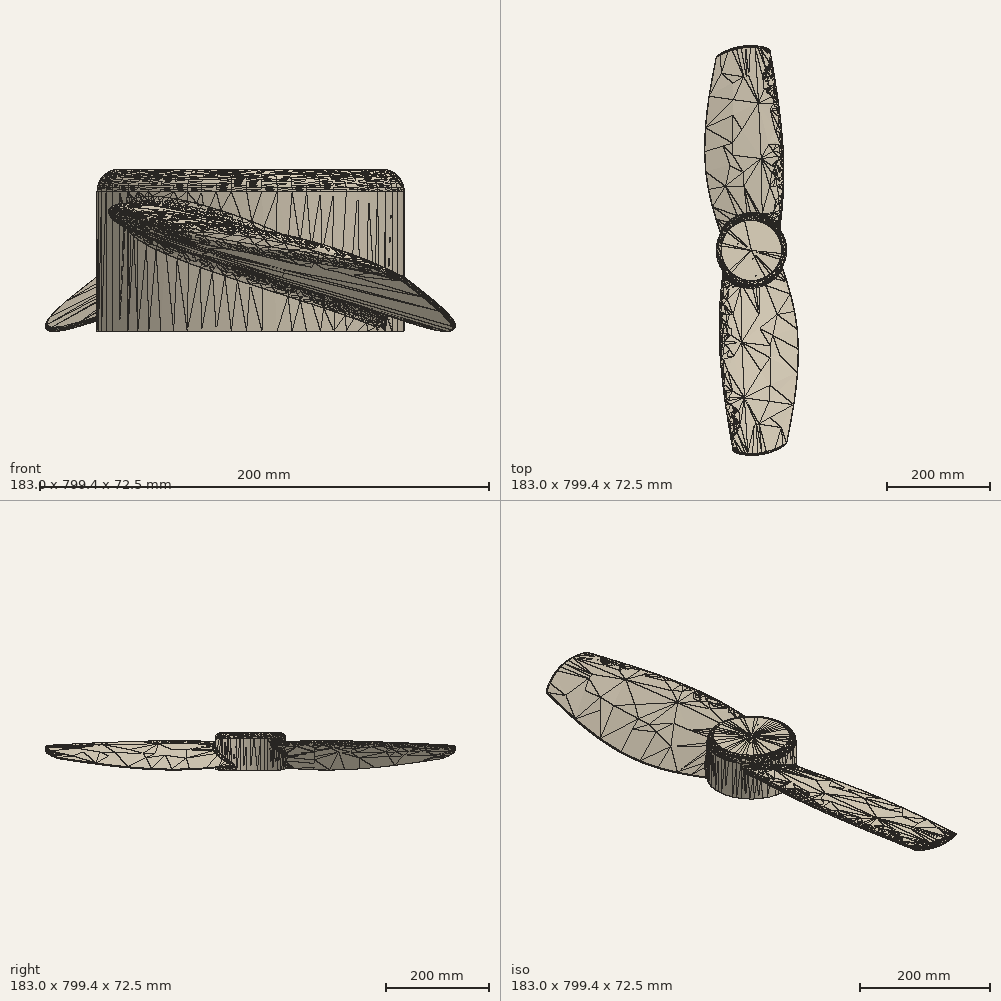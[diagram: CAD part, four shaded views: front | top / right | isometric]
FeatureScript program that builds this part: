
annotation { "Feature Type Name" : "Feature", "Feature Type Description" : "" }
export const myFeature = defineFeature(function(context is Context, id is Id, definition is map)
    precondition{}
    {
        {
            var Q0;
            Q0=qCreatedBy(makeId("Front.planeOp"),FACE);
            var sketch = newSketch(context, id + "F0", { "sketchPlane" : qUnion([Q0])});
            skLineSegment(sketch, "E0", {"start": v(-25.68, 10.16) * mm, "end": v(0, 0) * mm, "construction": true});
            skLineSegment(sketch, "E1", {"start": v(0, 0) * mm, "end": v(25.68, -10.16) * mm, "construction": true});
            skLineSegment(sketch, "E2", {"start": v(25.68, -10.16) * mm, "end": v(51.36, -20.31) * mm, "construction": true});
            skLineSegment(sketch, "E3", {"start": v(51.36, -20.31) * mm, "end": v(77.03, -30.47) * mm, "construction": true});
            skLineSegment(sketch, "E4", {"start": v(0, 0) * mm, "end": v(3.73, 9.44) * mm, "construction": true});
            skLineSegment(sketch, "E5", {"start": v(-25.68, 10.16) * mm, "end": v(-23.81, 14.88) * mm, "construction": true});
            skFitSpline(sketch, "E6", {"points": [v(-25.68, 10.16) * mm, v(3.73, 9.44) * mm, v(77.03, -30.47) * mm], "startDerivative": vector(15.03, 38) * mm, "endDerivative": vector(104.92, -93.69) * mm});
            skPoint(sketch, "E7", {"position": v(1.87, 4.72) * mm});
            skLineSegment(sketch, "E8", {"start": v(-23.81, 14.88) * mm, "end": v(1.87, 4.72) * mm, "construction": true});
            skLineSegment(sketch, "E9", {"start": v(0, 0) * mm, "end": v(-1.87, -4.72) * mm, "construction": true});
            skLineSegment(sketch, "E10", {"start": v(-25.68, 10.16) * mm, "end": v(-27.54, 5.44) * mm, "construction": true});
            skFitSpline(sketch, "E11", {"points": [v(-25.68, 10.16) * mm, v(-1.87, -4.72) * mm, v(77.03, -30.47) * mm], "startDerivative": vector(-15.23, -38.5) * mm, "endDerivative": vector(121.84, -48.19) * mm});
            skLineSegment(sketch, "E12", {"start": v(51.36, -20.31) * mm, "end": v(55.09, -10.87) * mm, "construction": true});
            skSolve(sketch);
        }
        {
            var Q0;
            Q0=qCreatedBy(makeId("Front.planeOp"),FACE);
            cPlane(context, id + "F1", {"entities" : qUnion([Q0]), "cplaneType" : CPlaneType.OFFSET, "offset" : 125 * mm, "width" : 150 * mm, "height" : 150 * mm});
        }
        {
            var Q0;
            Q0=qCreatedBy(id+"F1.planeOp",FACE);
            var sketch = newSketch(context, id + "F2", { "sketchPlane" : qUnion([Q0])});
            skLineSegment(sketch, "E13", {"start": v(-38.33, 14.06) * mm, "end": v(0, 0) * mm, "construction": true});
            skLineSegment(sketch, "E14", {"start": v(0, 0) * mm, "end": v(38.33, -14.06) * mm, "construction": true});
            skLineSegment(sketch, "E15", {"start": v(38.33, -14.06) * mm, "end": v(76.67, -28.12) * mm, "construction": true});
            skLineSegment(sketch, "E16", {"start": v(76.67, -28.12) * mm, "end": v(115, -42.17) * mm, "construction": true});
            skLineSegment(sketch, "E17", {"start": v(0, 0) * mm, "end": v(4.06, 11.06) * mm, "construction": true});
            skLineSegment(sketch, "E18", {"start": v(-38.33, 14.06) * mm, "end": v(-36.3, 19.59) * mm, "construction": true});
            skFitSpline(sketch, "E19", {"points": [v(-38.33, 14.06) * mm, v(4.06, 11.06) * mm, v(115, -42.17) * mm], "startDerivative": vector(16.44, 44.82) * mm, "endDerivative": vector(163.27, -119.63) * mm});
            skPoint(sketch, "E20", {"position": v(2.03, 5.53) * mm});
            skLineSegment(sketch, "E21", {"start": v(-36.3, 19.59) * mm, "end": v(2.03, 5.53) * mm, "construction": true});
            skLineSegment(sketch, "E22", {"start": v(0, 0) * mm, "end": v(-2.03, -5.53) * mm, "construction": true});
            skLineSegment(sketch, "E23", {"start": v(-38.33, 14.06) * mm, "end": v(-40.36, 8.53) * mm, "construction": true});
            skFitSpline(sketch, "E24", {"points": [v(-38.33, 14.06) * mm, v(-2.03, -5.53) * mm, v(115, -42.17) * mm], "startDerivative": vector(-16.57, -45.19) * mm, "endDerivative": vector(181.7, -66.64) * mm});
            skLineSegment(sketch, "E25", {"start": v(76.67, -28.12) * mm, "end": v(80.72, -17.06) * mm, "construction": true});
            skSolve(sketch);
        }
        {
            var Q0;
            Q0=qCreatedBy(makeId("Front.planeOp"),FACE);
            cPlane(context, id + "F3", {"entities" : qUnion([Q0]), "cplaneType" : CPlaneType.OFFSET, "offset" : 400 * mm, "width" : 150 * mm, "height" : 150 * mm});
        }
        {
            var Q0;
            Q0=qCreatedBy(id+"F3.planeOp",FACE);
            var sketch = newSketch(context, id + "F4", { "sketchPlane" : qUnion([Q0])});
            skLineSegment(sketch, "E26", {"start": v(-10.03, 5.14) * mm, "end": v(16.27, 0) * mm, "construction": true});
            skLineSegment(sketch, "E27", {"start": v(16.27, 0) * mm, "end": v(42.56, -5.14) * mm, "construction": true});
            skLineSegment(sketch, "E28", {"start": v(42.56, -5.14) * mm, "end": v(68.86, -10.28) * mm, "construction": true});
            skLineSegment(sketch, "E29", {"start": v(68.86, -10.28) * mm, "end": v(95.16, -15.42) * mm, "construction": true});
            skLineSegment(sketch, "E30", {"start": v(16.27, 0) * mm, "end": v(17.61, 6.9) * mm, "construction": true});
            skLineSegment(sketch, "E31", {"start": v(-10.03, 5.14) * mm, "end": v(-9.36, 8.59) * mm, "construction": true});
            skFitSpline(sketch, "E32", {"points": [v(-10.03, 5.14) * mm, v(17.61, 6.9) * mm, v(95.16, -15.42) * mm], "startDerivative": vector(5.47, 28.01) * mm, "endDerivative": vector(118.7, -57.28) * mm});
            skPoint(sketch, "E33", {"position": v(16.94, 3.45) * mm});
            skLineSegment(sketch, "E34", {"start": v(-9.36, 8.59) * mm, "end": v(16.94, 3.45) * mm, "construction": true});
            skLineSegment(sketch, "E35", {"start": v(16.27, 0) * mm, "end": v(15.6, -3.45) * mm, "construction": true});
            skLineSegment(sketch, "E36", {"start": v(-10.03, 5.14) * mm, "end": v(-10.7, 1.7) * mm, "construction": true});
            skFitSpline(sketch, "E37", {"points": [v(-10.03, 5.14) * mm, v(15.6, -3.45) * mm, v(95.16, -15.42) * mm], "startDerivative": vector(-5.51, -28.2) * mm, "endDerivative": vector(124.61, -24.36) * mm});
            skLineSegment(sketch, "E38", {"start": v(68.86, -10.28) * mm, "end": v(70.2, -3.38) * mm, "construction": true});
            skSolve(sketch);
        }
        {
            var Q0;
            Q0=qSketchRegion(id+"F0",true);
            var Q1;
            Q1=qSketchRegion(id+"F2",true);
            var Q2;
            Q2=qSketchRegion(id+"F4",true);
            var Q3;
            Q3=sQuery(id+"F0.wireOp",VERTEX,"E6.1.internal");
            var Q4;
            Q4=sQuery(id+"F2.wireOp",VERTEX,"E19.1.internal");
            var Q5;
            Q5=sQuery(id+"F4.wireOp",VERTEX,"E30.end");
            loft(context, id + "F5", {"sheetProfilesArray" : [{ "sheetProfileEntities" : qUnion([Q0]) }, { "sheetProfileEntities" : qUnion([Q1]) }, { "sheetProfileEntities" : qUnion([Q2]) }], "matchConnections" : true, "connections" : [{ "connectionEntities" : qUnion([Q3, Q4, Q5]), "connectionEdgeQueries" : qUnion([]), "connectionEdgeParameters" : [] }]});
        }
        {
            var Q0;
            Q0=qCreatedBy(makeId("Top.planeOp"),FACE);
            var sketch = newSketch(context, id + "F6", { "sketchPlane" : qUnion([Q0])});
            skFitSpline(sketch, "E39", {"points": [v(-55.98, -360.47) * mm, v(39.38, -398.87) * mm, v(142.8, -333.19) * mm], "startDerivative": vector(111.22, -150.8) * mm, "endDerivative": vector(54.24, 145.78) * mm});
            skLineSegment(sketch, "E40", {"start": v(-55.98, -360.47) * mm, "end": v(-55.98, -458.75) * mm});
            skLineSegment(sketch, "E41", {"start": v(142.8, -333.19) * mm, "end": v(142.8, -458.75) * mm});
            skLineSegment(sketch, "E42", {"start": v(142.8, -458.75) * mm, "end": v(-55.98, -458.75) * mm});
            skSolve(sketch);
        }
        {
            var Q0;
            Q0=qSketchRegion(id+"F6",true);
            extrude(context, id + "F7", {"entities" : qUnion([Q0]), "operationType" : NewBodyOperationType.REMOVE, "endBound" : BoundingType.SYMMETRIC, "oppositeDirection" : true, "depth" : 40.17 * mm});
        }
        {
            var Q0;
            Q0=makeQuery(id+"F5.opLoft","SWEPT_EDGE",EDGE,{"disambiguationData":[OSD([sQuery(id+"F2.wireOp",EDGE,"E19"),sQuery(id+"F2.wireOp",EDGE,"E24"),sQuery(id+"F4.wireOp",EDGE,"E32"),sQuery(id+"F4.wireOp",EDGE,"E37")])]});
            fillet(context, id + "F8", {"entities" : qUnion([Q0]), "radius" : 1 * mm, "tangentPropagation" : true, "allowEdgeOverflow" : false});
        }
        {
            var Q0;
            Q0=makeQuery(id+"F7.boolean.opBoolean","COPY",FACE,{"derivedFrom":makeQuery(id+"F7.opExtrude","SWEPT_FACE",FACE,{"disambiguationData":[OSD([sQuery(id+"F6.wireOp",EDGE,"E39")])]})});
            fillet(context, id + "F9", {"entities" : qUnion([Q0]), "radius" : 4 * mm, "tangentPropagation" : true, "allowEdgeOverflow" : false});
        }
        {
            var Q0;
            Q0=qCreatedBy(makeId("Top.planeOp"),FACE);
            var sketch = newSketch(context, id + "F10", { "sketchPlane" : qUnion([Q0])});
            skCircle(sketch, "E43", {"center": v(24.35, 0) * mm, "radius": 68.6 * mm});
            skSolve(sketch);
        }
        {
            var Q0;
            Q0=qSketchRegion(id+"F10",true);
            extrude(context, id + "F11", {"entities" : qUnion([Q0]), "depth" : 32.31 * mm, "hasSecondDirection" : true, "secondDirectionOppositeDirection" : true, "secondDirectionDepth" : 40 * mm});
        }
        {
            var Q0;
            Q0=makeQuery(id+"F5.opLoft","SWEPT_BODY",BODY,{"disambiguationData":[OSD([makeQuery(id+"F0.imprint","IMPRINT",FACE,{"disambiguationData":[TD([[makeQuery(id+"F0.imprint","IMPRINT",EDGE,{"derivedFrom":sQuery(id+"F0.wireOp",EDGE,"E6")}),-1.0]])]}),sQuery(id+"F2.wireOp",EDGE,"E24"),makeQuery(id+"F4.imprint","IMPRINT",FACE,{"disambiguationData":[TD([[makeQuery(id+"F4.imprint","IMPRINT",EDGE,{"derivedFrom":sQuery(id+"F4.wireOp",EDGE,"E32")}),-1.0]])]})])]});
            var Q1;
            Q1=makeQuery(id+"F11.opExtrude","SWEPT_FACE",FACE,{"disambiguationData":[OSD([sQuery(id+"F10.wireOp",EDGE,"E43")])]});
            circularPattern(context, id + "F12", {"entities" : qUnion([Q0]), "axis" : qUnion([Q1]), "angle" : 360 * degree, "instanceCount" : 2, "equalSpace" : true});
        }
        {
            var Q0;
            Q0=makeQuery(id+"F12.opPattern","COPY",BODY,{"derivedFrom":makeQuery(id+"F5.opLoft","SWEPT_BODY",BODY,{"disambiguationData":[OSD([makeQuery(id+"F0.imprint","IMPRINT",FACE,{"disambiguationData":[TD([[makeQuery(id+"F0.imprint","IMPRINT",EDGE,{"derivedFrom":sQuery(id+"F0.wireOp",EDGE,"E6")}),-1.0]])]}),sQuery(id+"F2.wireOp",EDGE,"E24"),makeQuery(id+"F4.imprint","IMPRINT",FACE,{"disambiguationData":[TD([[makeQuery(id+"F4.imprint","IMPRINT",EDGE,{"derivedFrom":sQuery(id+"F4.wireOp",EDGE,"E32")}),-1.0]])]})])]}),"instanceName":"2"});
            var Q1;
            Q1=makeQuery(id+"F5.opLoft","SWEPT_BODY",BODY,{"disambiguationData":[OSD([makeQuery(id+"F0.imprint","IMPRINT",FACE,{"disambiguationData":[TD([[makeQuery(id+"F0.imprint","IMPRINT",EDGE,{"derivedFrom":sQuery(id+"F0.wireOp",EDGE,"E6")}),-1.0]])]}),sQuery(id+"F2.wireOp",EDGE,"E24"),makeQuery(id+"F4.imprint","IMPRINT",FACE,{"disambiguationData":[TD([[makeQuery(id+"F4.imprint","IMPRINT",EDGE,{"derivedFrom":sQuery(id+"F4.wireOp",EDGE,"E32")}),-1.0]])]})])]});
            var Q2;
            Q2=makeQuery(id+"F11.opExtrude","SWEPT_BODY",BODY,{"disambiguationData":[OSD([sQuery(id+"F10.wireOp",EDGE,"E43")])]});
            var Q3;
            Q3=makeQuery(id+"F12.opPattern","COPY",BODY,{"derivedFrom":makeQuery(id+"F5.opLoft","SWEPT_BODY",BODY,{"disambiguationData":[OSD([makeQuery(id+"F0.imprint","IMPRINT",FACE,{"disambiguationData":[TD([[makeQuery(id+"F0.imprint","IMPRINT",EDGE,{"derivedFrom":sQuery(id+"F0.wireOp",EDGE,"E6")}),-1.0]])]}),sQuery(id+"F2.wireOp",EDGE,"E24"),makeQuery(id+"F4.imprint","IMPRINT",FACE,{"disambiguationData":[TD([[makeQuery(id+"F4.imprint","IMPRINT",EDGE,{"derivedFrom":sQuery(id+"F4.wireOp",EDGE,"E32")}),-1.0]])]})])]}),"instanceName":"1"});
            var Q4;
            Q4=makeQuery(id+"F12.opPattern","COPY",BODY,{"derivedFrom":makeQuery(id+"F5.opLoft","SWEPT_BODY",BODY,{"disambiguationData":[OSD([makeQuery(id+"F0.imprint","IMPRINT",FACE,{"disambiguationData":[TD([[makeQuery(id+"F0.imprint","IMPRINT",EDGE,{"derivedFrom":sQuery(id+"F0.wireOp",EDGE,"E6")}),-1.0]])]}),sQuery(id+"F2.wireOp",EDGE,"E24"),makeQuery(id+"F4.imprint","IMPRINT",FACE,{"disambiguationData":[TD([[makeQuery(id+"F4.imprint","IMPRINT",EDGE,{"derivedFrom":sQuery(id+"F4.wireOp",EDGE,"E32")}),-1.0]])]})])]}),"instanceName":"4"});
            var Q5;
            Q5=makeQuery(id+"F12.opPattern","COPY",BODY,{"derivedFrom":makeQuery(id+"F5.opLoft","SWEPT_BODY",BODY,{"disambiguationData":[OSD([makeQuery(id+"F0.imprint","IMPRINT",FACE,{"disambiguationData":[TD([[makeQuery(id+"F0.imprint","IMPRINT",EDGE,{"derivedFrom":sQuery(id+"F0.wireOp",EDGE,"E6")}),-1.0]])]}),sQuery(id+"F2.wireOp",EDGE,"E24"),makeQuery(id+"F4.imprint","IMPRINT",FACE,{"disambiguationData":[TD([[makeQuery(id+"F4.imprint","IMPRINT",EDGE,{"derivedFrom":sQuery(id+"F4.wireOp",EDGE,"E32")}),-1.0]])]})])]}),"instanceName":"3"});
            booleanBodies(context, id + "F13", {"operationType" : BooleanOperationType.UNION, "tools" : qUnion([Q0, Q1, Q2, Q3, Q4, Q5])});
        }
        {
            var Q0;
            Q0=makeQuery(id+"F11.opExtrude","CAP_FACE",FACE,{"disambiguationData":[OSD([sQuery(id+"F10.wireOp",EDGE,"E43")])],"isStart":false});
            var sketch = newSketch(context, id + "F14", { "sketchPlane" : qUnion([Q0])});
            skCircle(sketch, "E44", {"center": v(24.35, 0) * mm, "radius": 0.5 * mm});
            skSolve(sketch);
        }
        {
            var Q0;
            Q0=qSketchRegion(id+"F14",true);
            extrude(context, id + "F15", {"entities" : qUnion([Q0]), "operationType" : NewBodyOperationType.REMOVE, "endBound" : BoundingType.THROUGH_ALL, "oppositeDirection" : true, "depth" : 25 * mm});
        }
        {
            var Q0;
            {var subQ0=sQuery(id+"F0.wireOp",VERTEX,"E6.1.internal");var subQ1=sQuery(id+"F0.wireOp",EDGE,"E6");var subQ2=sQuery(id+"F0.wireOp",EDGE,"E11");var subQ3=sQuery(id+"F2.wireOp",VERTEX,"E19.1.internal");var subQ4=sQuery(id+"F2.wireOp",EDGE,"E19");var subQ5=sQuery(id+"F2.wireOp",EDGE,"E24");Q0=makeQuery(id+"F13.opBoolean","INTERSECT",EDGE,{"derivedFrom":[makeQuery(id+"F11.opExtrude","SWEPT_FACE",FACE,{"disambiguationData":[OSD([sQuery(id+"F10.wireOp",EDGE,"E43")])]}),makeQuery(id+"F12.opPattern","COPY",FACE,{"derivedFrom":makeQuery(id+"F5.opLoft","SWEPT_FACE",FACE,{"disambiguationData":[OSD([subQ0,subQ1,subQ2,subQ3,subQ4,subQ5]),TDD([subQ0,makeQuery(id+"F0.imprint","INTERSECT",VERTEX,{"disambiguationData":[OD(0.0)],"derivedFrom":[subQ1,subQ2]}),makeQuery(id+"F0.imprint","IMPRINT",EDGE,{"derivedFrom":subQ1}),subQ3,makeQuery(id+"F2.imprint","INTERSECT",VERTEX,{"disambiguationData":[OD(0.0)],"derivedFrom":[subQ4,subQ5]}),makeQuery(id+"F2.imprint","IMPRINT",EDGE,{"derivedFrom":subQ4})])]}),"instanceName":"2"})]});}
            var Q1;
            {var subQ0=sQuery(id+"F0.wireOp",VERTEX,"E6.1.internal");var subQ1=sQuery(id+"F0.wireOp",EDGE,"E6");var subQ2=sQuery(id+"F0.wireOp",EDGE,"E11");var subQ3=sQuery(id+"F2.wireOp",VERTEX,"E19.1.internal");var subQ4=sQuery(id+"F2.wireOp",EDGE,"E19");var subQ5=sQuery(id+"F2.wireOp",EDGE,"E24");Q1=makeQuery(id+"F13.opBoolean","INTERSECT",EDGE,{"derivedFrom":[makeQuery(id+"F5.opLoft","SWEPT_FACE",FACE,{"disambiguationData":[OSD([subQ0,subQ1,subQ2,subQ3,subQ4,subQ5]),TDD([subQ0,makeQuery(id+"F0.imprint","INTERSECT",VERTEX,{"disambiguationData":[OD(1.0)],"derivedFrom":[subQ1,subQ2]}),makeQuery(id+"F0.imprint","IMPRINT",EDGE,{"derivedFrom":subQ1}),subQ3,makeQuery(id+"F2.imprint","INTERSECT",VERTEX,{"disambiguationData":[OD(1.0)],"derivedFrom":[subQ4,subQ5]}),makeQuery(id+"F2.imprint","IMPRINT",EDGE,{"derivedFrom":subQ4})])]}),makeQuery(id+"F11.opExtrude","SWEPT_FACE",FACE,{"disambiguationData":[OSD([sQuery(id+"F10.wireOp",EDGE,"E43")])]})]});}
            var Q2;
            {var subQ0=sQuery(id+"F0.wireOp",VERTEX,"E6.1.internal");var subQ1=sQuery(id+"F0.wireOp",EDGE,"E6");var subQ2=sQuery(id+"F0.wireOp",EDGE,"E11");var subQ3=sQuery(id+"F2.wireOp",VERTEX,"E19.1.internal");var subQ4=sQuery(id+"F2.wireOp",EDGE,"E19");var subQ5=sQuery(id+"F2.wireOp",EDGE,"E24");Q2=makeQuery(id+"F13.opBoolean","INTERSECT",EDGE,{"derivedFrom":[makeQuery(id+"F11.opExtrude","SWEPT_FACE",FACE,{"disambiguationData":[OSD([sQuery(id+"F10.wireOp",EDGE,"E43")])]}),makeQuery(id+"F12.opPattern","COPY",FACE,{"derivedFrom":makeQuery(id+"F5.opLoft","SWEPT_FACE",FACE,{"disambiguationData":[OSD([subQ0,subQ1,subQ2,subQ3,subQ4,subQ5]),TDD([subQ0,makeQuery(id+"F0.imprint","INTERSECT",VERTEX,{"disambiguationData":[OD(1.0)],"derivedFrom":[subQ1,subQ2]}),makeQuery(id+"F0.imprint","IMPRINT",EDGE,{"derivedFrom":subQ1}),subQ3,makeQuery(id+"F2.imprint","INTERSECT",VERTEX,{"disambiguationData":[OD(1.0)],"derivedFrom":[subQ4,subQ5]}),makeQuery(id+"F2.imprint","IMPRINT",EDGE,{"derivedFrom":subQ4})])]}),"instanceName":"1"})]});}
            var Q3;
            {var subQ0=sQuery(id+"F0.wireOp",VERTEX,"E6.1.internal");var subQ1=sQuery(id+"F0.wireOp",EDGE,"E6");var subQ2=sQuery(id+"F0.wireOp",EDGE,"E11");var subQ3=sQuery(id+"F2.wireOp",VERTEX,"E19.1.internal");var subQ4=sQuery(id+"F2.wireOp",EDGE,"E19");var subQ5=sQuery(id+"F2.wireOp",EDGE,"E24");Q3=makeQuery(id+"F13.opBoolean","INTERSECT",EDGE,{"derivedFrom":[makeQuery(id+"F11.opExtrude","SWEPT_FACE",FACE,{"disambiguationData":[OSD([sQuery(id+"F10.wireOp",EDGE,"E43")])]}),makeQuery(id+"F12.opPattern","COPY",FACE,{"derivedFrom":makeQuery(id+"F5.opLoft","SWEPT_FACE",FACE,{"disambiguationData":[OSD([subQ0,subQ1,subQ2,subQ3,subQ4,subQ5]),TDD([subQ0,makeQuery(id+"F0.imprint","INTERSECT",VERTEX,{"disambiguationData":[OD(1.0)],"derivedFrom":[subQ1,subQ2]}),makeQuery(id+"F0.imprint","IMPRINT",EDGE,{"derivedFrom":subQ1}),subQ3,makeQuery(id+"F2.imprint","INTERSECT",VERTEX,{"disambiguationData":[OD(1.0)],"derivedFrom":[subQ4,subQ5]}),makeQuery(id+"F2.imprint","IMPRINT",EDGE,{"derivedFrom":subQ4})])]}),"instanceName":"4"})]});}
            var Q4;
            {var subQ0=sQuery(id+"F0.wireOp",VERTEX,"E6.1.internal");var subQ1=sQuery(id+"F0.wireOp",EDGE,"E6");var subQ2=sQuery(id+"F0.wireOp",EDGE,"E11");var subQ3=sQuery(id+"F2.wireOp",VERTEX,"E19.1.internal");var subQ4=sQuery(id+"F2.wireOp",EDGE,"E19");var subQ5=sQuery(id+"F2.wireOp",EDGE,"E24");Q4=makeQuery(id+"F13.opBoolean","INTERSECT",EDGE,{"derivedFrom":[makeQuery(id+"F11.opExtrude","SWEPT_FACE",FACE,{"disambiguationData":[OSD([sQuery(id+"F10.wireOp",EDGE,"E43")])]}),makeQuery(id+"F12.opPattern","COPY",FACE,{"derivedFrom":makeQuery(id+"F5.opLoft","SWEPT_FACE",FACE,{"disambiguationData":[OSD([subQ0,subQ1,subQ2,subQ3,subQ4,subQ5]),TDD([subQ0,makeQuery(id+"F0.imprint","INTERSECT",VERTEX,{"disambiguationData":[OD(0.0)],"derivedFrom":[subQ1,subQ2]}),makeQuery(id+"F0.imprint","IMPRINT",EDGE,{"derivedFrom":subQ1}),subQ3,makeQuery(id+"F2.imprint","INTERSECT",VERTEX,{"disambiguationData":[OD(0.0)],"derivedFrom":[subQ4,subQ5]}),makeQuery(id+"F2.imprint","IMPRINT",EDGE,{"derivedFrom":subQ4})])]}),"instanceName":"3"})]});}
            fillet(context, id + "F16", {"entities" : qUnion([Q0, Q1, Q2, Q3, Q4]), "radius" : 5 * mm, "tangentPropagation" : true, "allowEdgeOverflow" : false});
        }
        {
            var Q0;
            Q0=makeQuery(id+"F11.opExtrude","CAP_EDGE",EDGE,{"disambiguationData":[OSD([sQuery(id+"F10.wireOp",EDGE,"E43")])],"isStart":false});
            fillet(context, id + "F17", {"entities" : qUnion([Q0]), "radius" : 10 * mm, "tangentPropagation" : true, "allowEdgeOverflow" : false});
        }
    });
